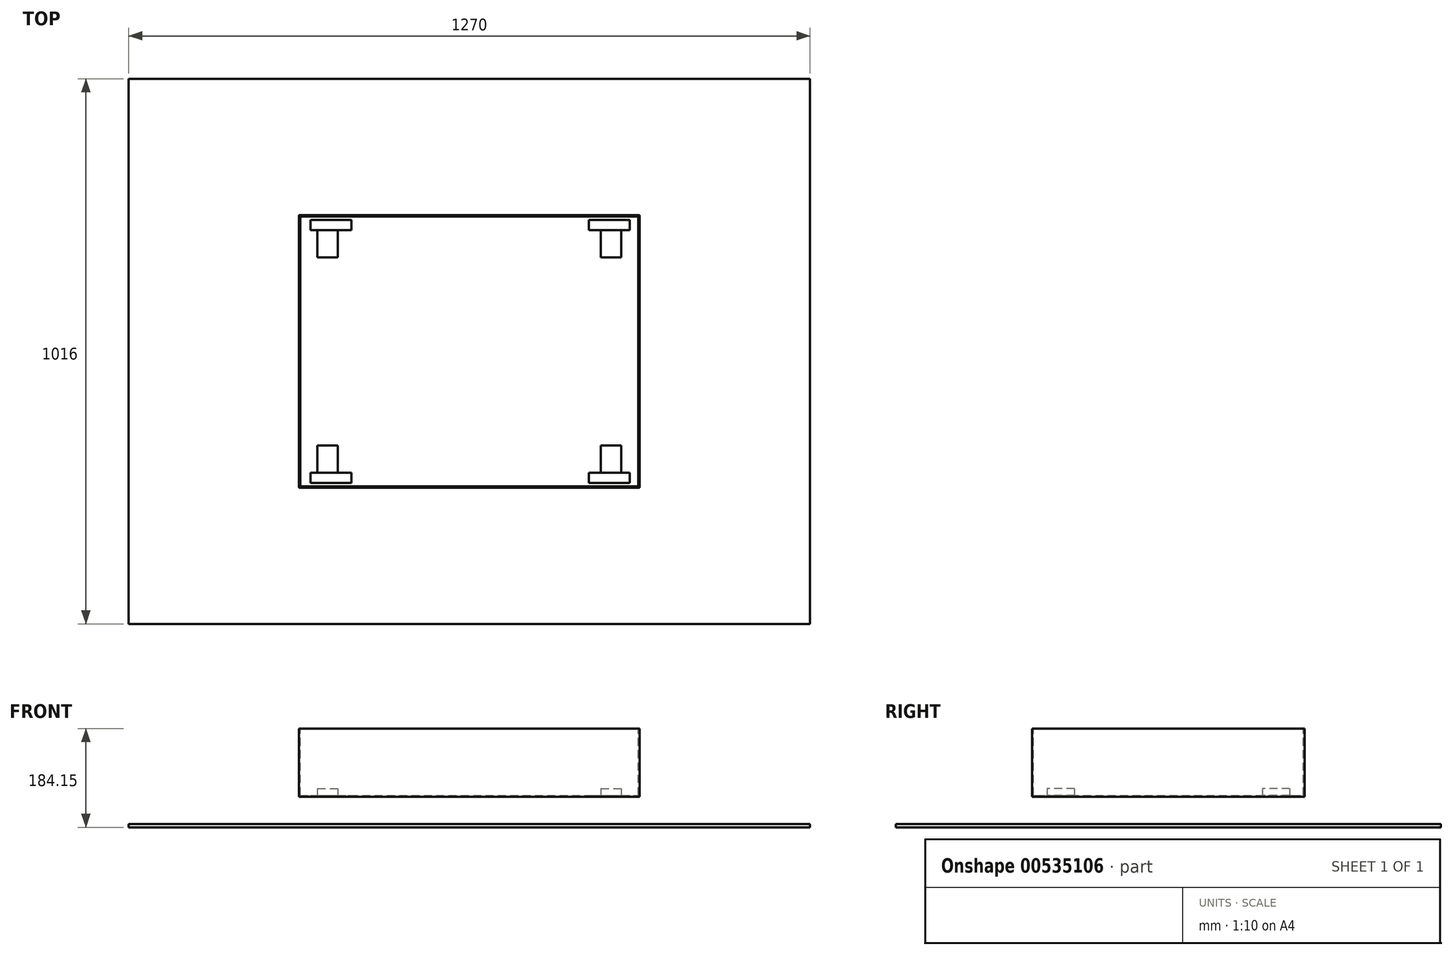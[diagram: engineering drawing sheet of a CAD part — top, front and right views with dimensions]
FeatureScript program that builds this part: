
annotation { "Feature Type Name" : "Feature", "Feature Type Description" : "" }
export const myFeature = defineFeature(function(context is Context, id is Id, definition is map)
    precondition{}
    {
        {
            var Q0;
            Q0=qCreatedBy(makeId("Front.planeOp"),FACE);
            var sketch = newSketch(context, id + "F0", { "sketchPlane" : qUnion([Q0])});
            skLineSegment(sketch, "E0.bottom", {"start": v(0, 0) * mm, "end": v(635, 0) * mm});
            skLineSegment(sketch, "E0.top", {"start": v(0, 127) * mm, "end": v(635, 127) * mm});
            skLineSegment(sketch, "E0.left", {"start": v(0, 0) * mm, "end": v(0, 127) * mm});
            skLineSegment(sketch, "E0.right", {"start": v(635, 0) * mm, "end": v(635, 127) * mm});
            skSolve(sketch);
        }
        {
            var Q0;
            Q0=qSketchRegion(id+"F0",true);
            extrude(context, id + "F1", {"entities" : qUnion([Q0]), "depth" : 508 * mm});
        }
        {
            var Q0;
            Q0=makeQuery(id+"F1.opExtrude","SWEPT_FACE",FACE,{"disambiguationData":[OSD([sQuery(id+"F0.wireOp",EDGE,"E0.top")])]});
            shell(context, id + "F2", {"entities" : qUnion([Q0]), "thickness" : 2.54 * mm});
        }
        {
            var Q0;
            Q0=makeQuery(id+"F2.opShell","OFFSET_FACE",FACE,{"disambiguationData":[OSD([sQuery(id+"F0.wireOp",EDGE,"E0.bottom")])]});
            var sketch = newSketch(context, id + "F3", { "sketchPlane" : qUnion([Q0])});
            skLineSegment(sketch, "E1.bottom", {"start": v(34.3, -27.94) * mm, "end": v(72.39, -27.94) * mm});
            skLineSegment(sketch, "E1.top", {"start": v(34.3, -78.74) * mm, "end": v(72.4, -78.74) * mm});
            skLineSegment(sketch, "E1.left", {"start": v(34.3, -27.94) * mm, "end": v(34.3, -78.74) * mm});
            skLineSegment(sketch, "E1.right", {"start": v(72.4, -27.94) * mm, "end": v(72.4, -78.74) * mm});
            skLineSegment(sketch, "E2.bottom", {"start": v(2.54, -2.54) * mm, "end": v(34.3, -2.54) * mm});
            skLineSegment(sketch, "E2.top", {"start": v(2.54, -27.94) * mm, "end": v(34.3, -27.94) * mm});
            skLineSegment(sketch, "E2.left", {"start": v(2.54, -2.54) * mm, "end": v(2.54, -27.94) * mm});
            skLineSegment(sketch, "E2.right", {"start": v(34.3, -2.54) * mm, "end": v(34.3, -27.94) * mm});
            skLineSegment(sketch, "E3.0.1.0", {"start": v(34.3, -429.26) * mm, "end": v(72.39, -429.26) * mm});
            skLineSegment(sketch, "E3.0.1.1", {"start": v(34.3, -429.26) * mm, "end": v(34.3, -480.06) * mm});
            skLineSegment(sketch, "E3.0.1.2", {"start": v(34.3, -480.06) * mm, "end": v(72.39, -480.06) * mm});
            skLineSegment(sketch, "E3.0.1.3", {"start": v(72.4, -429.26) * mm, "end": v(72.4, -480.06) * mm});
            skLineSegment(sketch, "E3.1.0.0", {"start": v(562.61, -27.94) * mm, "end": v(600.7, -27.94) * mm});
            skLineSegment(sketch, "E3.1.0.1", {"start": v(562.61, -27.94) * mm, "end": v(562.61, -78.74) * mm});
            skLineSegment(sketch, "E3.1.0.2", {"start": v(562.61, -78.74) * mm, "end": v(600.7, -78.74) * mm});
            skLineSegment(sketch, "E3.1.0.3", {"start": v(600.7, -27.94) * mm, "end": v(600.7, -78.74) * mm});
            skLineSegment(sketch, "E3.1.1.0", {"start": v(562.61, -429.26) * mm, "end": v(600.7, -429.26) * mm});
            skLineSegment(sketch, "E3.1.1.1", {"start": v(562.61, -429.26) * mm, "end": v(562.61, -480.06) * mm});
            skLineSegment(sketch, "E3.1.1.2", {"start": v(562.61, -480.06) * mm, "end": v(600.7, -480.06) * mm});
            skLineSegment(sketch, "E3.1.1.3", {"start": v(600.7, -429.26) * mm, "end": v(600.7, -480.06) * mm});
            skLineSegment(sketch, "E3.direction1", {"start": v(34.3, -27.94) * mm, "end": v(562.61, -27.94) * mm, "construction": true});
            skLineSegment(sketch, "E3.direction2", {"start": v(34.3, -27.94) * mm, "end": v(34.3, -429.26) * mm, "construction": true});
            skLineSegment(sketch, "E4.bottom", {"start": v(21.59, -499.1) * mm, "end": v(97.8, -499.1) * mm});
            skLineSegment(sketch, "E4.top", {"start": v(21.59, -480.06) * mm, "end": v(97.8, -480.06) * mm});
            skLineSegment(sketch, "E4.left", {"start": v(21.59, -499.1) * mm, "end": v(21.59, -480.06) * mm});
            skLineSegment(sketch, "E4.right", {"start": v(97.8, -499.1) * mm, "end": v(97.8, -480.06) * mm});
            skLineSegment(sketch, "E5.0.1.0", {"start": v(21.59, -8.9) * mm, "end": v(97.79, -8.9) * mm});
            skLineSegment(sketch, "E5.0.1.1", {"start": v(21.59, -27.94) * mm, "end": v(21.59, -8.9) * mm});
            skLineSegment(sketch, "E5.0.1.2", {"start": v(21.59, -27.94) * mm, "end": v(97.8, -27.94) * mm});
            skLineSegment(sketch, "E5.0.1.3", {"start": v(97.8, -27.94) * mm, "end": v(97.8, -8.9) * mm});
            skLineSegment(sketch, "E5.1.0.0", {"start": v(540.38, -480.06) * mm, "end": v(616.59, -480.06) * mm});
            skLineSegment(sketch, "E5.1.0.1", {"start": v(540.38, -499.1) * mm, "end": v(540.38, -480.06) * mm});
            skLineSegment(sketch, "E5.1.0.2", {"start": v(540.38, -499.1) * mm, "end": v(616.59, -499.1) * mm});
            skLineSegment(sketch, "E5.1.0.3", {"start": v(616.59, -499.1) * mm, "end": v(616.59, -480.06) * mm});
            skLineSegment(sketch, "E5.1.1.0", {"start": v(540.38, -8.9) * mm, "end": v(616.59, -8.9) * mm});
            skLineSegment(sketch, "E5.1.1.1", {"start": v(540.38, -27.94) * mm, "end": v(540.38, -8.9) * mm});
            skLineSegment(sketch, "E5.1.1.2", {"start": v(540.38, -27.94) * mm, "end": v(616.59, -27.94) * mm});
            skLineSegment(sketch, "E5.1.1.3", {"start": v(616.59, -27.94) * mm, "end": v(616.59, -8.9) * mm});
            skLineSegment(sketch, "E5.direction1", {"start": v(21.59, -480.06) * mm, "end": v(540.38, -480.06) * mm, "construction": true});
            skLineSegment(sketch, "E5.direction2", {"start": v(21.59, -480.06) * mm, "end": v(21.59, -8.9) * mm, "construction": true});
            skLineSegment(sketch, "E6", {"start": v(600.7, -27.94) * mm, "end": v(632.46, -27.94) * mm});
            skLineSegment(sketch, "E7", {"start": v(317.5, -505.46) * mm, "end": v(317.5, -2.54) * mm, "construction": true});
            skLineSegment(sketch, "E8", {"start": v(2.54, -254) * mm, "end": v(632.46, -254) * mm, "construction": true});
            skSolve(sketch);
        }
        {
            var Q0;
            Q0=makeQuery(id+"F3.imprint","IMPRINT",FACE,{"disambiguationData":[TD([[makeQuery(id+"F3.imprint","IMPRINT",EDGE,{"derivedFrom":sQuery(id+"F3.wireOp",EDGE,"E1.bottom")}),-1.0]])]});
            var Q1;
            Q1=makeQuery(id+"F3.imprint","IMPRINT",FACE,{"disambiguationData":[TD([[makeQuery(id+"F3.imprint","IMPRINT",EDGE,{"derivedFrom":sQuery(id+"F3.wireOp",EDGE,"E3.1.0.0")}),-1.0]])]});
            var Q2;
            Q2=makeQuery(id+"F3.imprint","IMPRINT",FACE,{"disambiguationData":[TD([[makeQuery(id+"F3.imprint","IMPRINT",EDGE,{"derivedFrom":sQuery(id+"F3.wireOp",EDGE,"E3.1.1.0")}),-1.0]])]});
            var Q3;
            Q3=makeQuery(id+"F3.imprint","IMPRINT",FACE,{"disambiguationData":[TD([[makeQuery(id+"F3.imprint","IMPRINT",EDGE,{"derivedFrom":sQuery(id+"F3.wireOp",EDGE,"E3.0.1.0")}),-1.0]])]});
            var Q4;
            Q4=makeQuery(id+"F3.imprint","IMPRINT",FACE,{"disambiguationData":[TD([[makeQuery(id+"F3.imprint","IMPRINT",EDGE,{"derivedFrom":sQuery(id+"F3.wireOp",EDGE,"E1.top")}),1.0]])]});
            var Q5;
            {var subQ0=sQuery(id+"F3.wireOp",EDGE,"E3.1.0.1");Q5=makeQuery(id+"F3.imprint","IMPRINT",FACE,{"disambiguationData":[TD([[makeQuery(id+"F3.imprint","IMPRINT",EDGE,{"derivedFrom":subQ0}),1.0]])]});}
            extrude(context, id + "F4", {"entities" : qUnion([Q0, Q1, Q2, Q3, Q4, Q5]), "operationType" : NewBodyOperationType.ADD, "depth" : 12.7 * mm});
        }
        {
            var Q0;
            Q0=makeQuery(id+"F3.imprint","IMPRINT",FACE,{"disambiguationData":[TD([[makeQuery(id+"F3.imprint","IMPRINT",EDGE,{"derivedFrom":sQuery(id+"F3.wireOp",EDGE,"E4.bottom")}),1.0]])]});
            var Q1;
            {var subQ2=sQuery(id+"F3.wireOp",EDGE,"E5.0.1.3");Q1=makeQuery(id+"F3.imprint","IMPRINT",FACE,{"disambiguationData":[TD([[makeQuery(id+"F3.imprint","IMPRINT",EDGE,{"derivedFrom":subQ2}),1.0]])]});}
            var Q2;
            {var subQ5=sQuery(id+"F3.wireOp",EDGE,"E5.0.1.1");Q2=makeQuery(id+"F3.imprint","IMPRINT",FACE,{"disambiguationData":[TD([[makeQuery(id+"F3.imprint","IMPRINT",EDGE,{"derivedFrom":subQ5}),-1.0]])]});}
            var Q3;
            Q3=makeQuery(id+"F3.imprint","IMPRINT",FACE,{"disambiguationData":[TD([[makeQuery(id+"F3.imprint","IMPRINT",EDGE,{"derivedFrom":sQuery(id+"F3.wireOp",EDGE,"E5.1.1.0")}),-1.0]])]});
            var Q4;
            {var subQ0=sQuery(id+"F3.wireOp",EDGE,"E5.1.0.1");Q4=makeQuery(id+"F3.imprint","IMPRINT",FACE,{"disambiguationData":[TD([[makeQuery(id+"F3.imprint","IMPRINT",EDGE,{"derivedFrom":subQ0}),-1.0]])]});}
            extrude(context, id + "F5", {"entities" : qUnion([Q0, Q1, Q2, Q3, Q4]), "operationType" : NewBodyOperationType.REMOVE, "oppositeDirection" : true, "depth" : 25.4 * mm});
        }
        {
            var Q0;
            Q0=makeQuery(id+"F1.opExtrude","SWEPT_FACE",FACE,{"disambiguationData":[OSD([sQuery(id+"F0.wireOp",EDGE,"E0.bottom")])]});
            cPlane(context, id + "F6", {"entities" : qUnion([Q0]), "cplaneType" : CPlaneType.OFFSET, "offset" : 50.8 * mm, "width" : 152.4 * mm, "height" : 152.4 * mm});
        }
        {
            var Q0;
            Q0=qCreatedBy(id+"F6.planeOp",FACE);
            var sketch = newSketch(context, id + "F7", { "sketchPlane" : qUnion([Q0])});
            skLineSegment(sketch, "E9.bottom", {"start": v(-317.5, 762) * mm, "end": v(952.5, 762) * mm});
            skLineSegment(sketch, "E9.top", {"start": v(-317.5, -254) * mm, "end": v(952.5, -254) * mm});
            skLineSegment(sketch, "E9.left", {"start": v(-317.5, 762) * mm, "end": v(-317.5, -254) * mm});
            skLineSegment(sketch, "E9.right", {"start": v(952.5, 762) * mm, "end": v(952.5, -254) * mm});
            skSolve(sketch);
        }
        {
            var Q0;
            Q0=makeQuery(id+"F7.imprint","IMPRINT",FACE,{"disambiguationData":[TD([[makeQuery(id+"F7.imprint","IMPRINT",EDGE,{"derivedFrom":sQuery(id+"F7.wireOp",EDGE,"E9.bottom")}),-1.0]])]});
            extrude(context, id + "F8", {"entities" : qUnion([Q0]), "depth" : 6.35 * mm});
        }
    });
